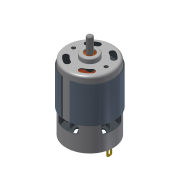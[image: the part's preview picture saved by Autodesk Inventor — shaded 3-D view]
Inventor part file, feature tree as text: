
AUTODESK INVENTOR PART (.ipt)
format: ipt  version: 2015 SP2 (Build 190223200, 223)  size: 657,920 bytes
history: native  units: mm
features: sketch x26, extrude x24, fillet x5, plane x4, hole x1, chamfer x1, mirror x1, pattern_circular x1, revolve x1
ambient origin geometry x8: Origin, YZ Plane, XZ Plane, XY Plane, X Axis, Y Axis, Z Axis, Center Point
bodies: Solid1 (feature_tree)
feature tree (64):
  extrude  "Extrusion1"  Depth=59.5mm TaperAngle=0.0deg
  extrude  "Extrusion2"  Depth=4.0mm TaperAngle=0.0deg
  extrude  "Extrusion3"  Depth=13.0mm TaperAngle=0.0deg
  hole  "Hole1"  [1 undecoded]
  fillet  "Fillet1"  Radius=1.0mm
  fillet  "Fillet2"  Radius=2.0mm
  fillet  "Fillet3"  Radius=29.0mm
  extrude  "Extrusion4"  Depth=1.0mm
  fillet  "Fillet4"  Radius=15.0mm
  extrude  "Extrusion5"  Depth=10.0mm
  extrude  "Extrusion6"  Depth=1.0mm
  extrude  "Extrusion7"  Depth=1.0mm
  fillet  "Fillet5"  Radius=1.0mm
  extrude  "Extrusion8"  Depth=2.35mm
  extrude  "Extrusion9"  Depth=0.5mm
  chamfer  "Chamfer1"  Distance=8.2mm
  extrude  "Extrusion10"  Depth=1.0mm TaperAngle=0.0deg
  mirror  "Mirror2"
  extrude  "Extrusion11"  Depth=1.0mm
  extrude  "Extrusion12"  Depth=1.0mm
  plane  "Work Plane1"
  extrude  "Extrusion13"  Depth=0.7mm TaperAngle=0.0deg
  pattern_circular  "Circular Pattern1"  Count=2 Angle=90.0deg
  plane  "Work Plane2"
  extrude  "Extrusion14"  Depth=40.4mm
  plane  "Work Plane3"
  extrude  "Extrusion15"  Depth=26.75mm
  extrude  "Extrusion16"  Depth=2.2mm TaperAngle=0.0deg
  extrude  "Extrusion17"  Depth=9.25mm
  extrude  "Extrusion18"  Depth=9.599311mm
  extrude  "Extrusion19"  Depth=2.2mm TaperAngle=0.0deg
  extrude  "Extrusion20"  Depth=29.0mm
  extrude  "Extrusion21"  Depth=32.0mm TaperAngle=0.0deg
  sketch  "Sketch23"  dims[d91=15.0deg d92=9.599311mm]
  revolve  "Revolution1"  [1 undecoded]
  extrude  "Extrusion22"  Depth=32.0mm TaperAngle=0.0deg
  extrude  "Extrusion23"  TaperAngle=90.0deg  [1 undecoded]
  plane  "Work Plane4"
  extrude  "Extrusion25"  Depth=32.0mm TaperAngle=0.0deg
  sketch  "Sketch1"  dims[d3=42.0mm d4=59.5mm d5=0.0mm]
  sketch  "Sketch2"  dims[d6=15.0mm d7=4.0mm d8=0.0mm]
  sketch  "Sketch3"  dims[d9=5.0mm d10=13.0mm d11=0.0mm]
  sketch  "Sketch4"  dims[d14=3.242mm d15=8.0mm d16=4.0mm d17=2.0mm d18=90.0deg d19=3.0mm d20=0.0mm d21=1.0mm d22=1.0mm d23=2.0mm d25=29.0mm]
  sketch  "Sketch5"  dims[d26=1.0mm d27=0.0mm d28=1.0mm d29=15.0mm]
  sketch  "Sketch6"  dims[d30=4.0mm d31=0.0mm d32=10.0mm]
  sketch  "Sketch7"  dims[d33=1.0mm d34=0.0mm d35=5.0mm]
  sketch  "Sketch8"  dims[d36=1.8mm d37=0.0mm d38=1.0mm d42=1.0mm d43=0.0mm]
  sketch  "Sketch9"  dims[d44=1.6mm d45=2.35mm]
  sketch  "Sketch10"  dims[d46=4.7mm d47=0.5mm d48=8.2mm d49=0.0mm]
  sketch  "Sketch11"  dims[d50=1.0mm d51=2.0mm d52=45.0deg d53=0.5mm d54=0.0mm]
  sketch  "Sketch12"  dims[d55=1.0mm d56=1.0mm]
  sketch  "Sketch13"  dims[d57=1.0mm d58=1.0mm]
  sketch  "Sketch14"  dims[d59=9.0mm d60=0.7mm d61=0.0mm]
  sketch  "Sketch15"  dims[d62=0.1mm d63=0.0mm]
  sketch  "Sketch16"  dims[d64=7.0mm]
  sketch  "Sketch17"  dims[d65=21.0mm]
  sketch  "Sketch18"  dims[d70=10.0mm d71=0.0mm d72=20.0mm d73=90.0deg]
  sketch  "Sketch19"  dims[d75=-28.0mm d76=40.4mm]
  sketch  "Sketch20"  dims[d77=54.75mm d78=0.0mm d79=26.75mm]
  sketch  "Sketch21"  dims[d80=4.0mm d81=2.2mm d82=0.0mm]
  sketch  "Sketch22"  dims[d88=2.2mm d89=0.0mm d90=9.25mm]
  sketch  "Sketch24"  dims[d93=2.5mm d94=2.2mm d95=0.0mm]
  sketch  "Sketch25"  dims[d96=0.6mm d97=0.0mm d98=29.0mm]
  sketch  "Sketch27"  dims[d99=20.0mm d100=0.0mm d101=66.0mm d102=0.0mm d103=23.2mm d104=8.75mm d105=0.0mm d109=90.0deg d117=5.0mm d118=0.0mm d119=8.2mm d120=12.25mm d121=0.0mm d126=-8.0mm d130=32.0mm d131=0.0mm]
note: 3 required parameter values undecoded (feature->parameter linkage not recoverable at this tier; creation-order binding heuristic only, values carry confidence <= 0.55)